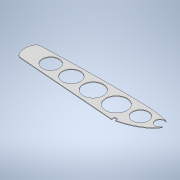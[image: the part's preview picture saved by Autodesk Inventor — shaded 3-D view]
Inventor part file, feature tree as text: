
AUTODESK INVENTOR PART (.ipt)
format: ipt  version: 2022 (Build 260153000, 153)  size: 228,352 bytes
history: native  units: mm
features: extrude x1, sketch x1
ambient origin geometry x8: Origin, YZ Plane, XZ Plane, XY Plane, X Axis, Y Axis, Z Axis, Center Point
bodies: Body1 (feature_tree)
feature tree (2):
  extrude  "Extrusion4"  Depth=1.0mm
  sketch  "Sketch1"  dims[d8=160.0mm d26=5.0mm d27=5.0mm d31=34.456mm d36=5.0mm d37=5.0mm d50=368.759386mm d51=15.0mm d52=28.0mm d53=31.0mm d54=26.0mm d57=15.0mm d59=33.0mm d63=1.0mm d64=0.0mm d65=44.669323mm d66=25.0mm d67=12.0mm d68=160.0mm d69=8.0mm d70=23.0mm d71=8.0mm d73=15.0mm d74=8.0mm d75=8.0mm d76=8.0mm]
